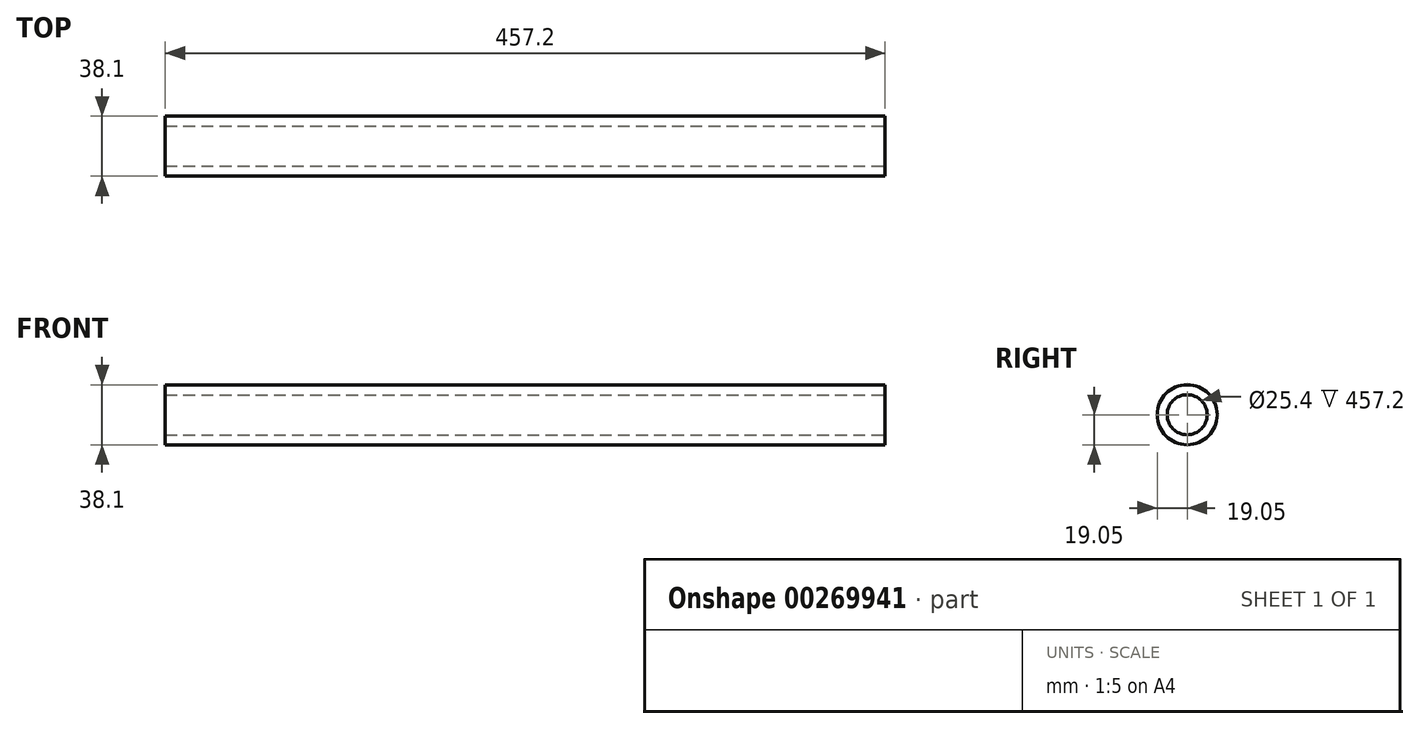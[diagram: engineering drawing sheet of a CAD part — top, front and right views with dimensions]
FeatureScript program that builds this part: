
annotation { "Feature Type Name" : "Feature", "Feature Type Description" : "" }
export const myFeature = defineFeature(function(context is Context, id is Id, definition is map)
    precondition{}
    {
        {
            var Q0;
            Q0=qCreatedBy(makeId("Right.planeOp"),FACE);
            var sketch = newSketch(context, id + "F0", { "sketchPlane" : qUnion([Q0])});
            skCircle(sketch, "E0", {"center": v(0, 0) * mm, "radius": 19.05 * mm});
            skSolve(sketch);
        }
        {
            var Q0;
            Q0=qSketchRegion(id+"F0",true);
            extrude(context, id + "F1", {"entities" : qUnion([Q0]), "depth" : 457.2 * mm});
        }
        {
            var Q0;
            Q0=makeQuery(id+"F1.opExtrude","CAP_FACE",FACE,{"disambiguationData":[OSD([sQuery(id+"F0.wireOp",EDGE,"E0")])],"isStart":false});
            var sketch = newSketch(context, id + "F2", { "sketchPlane" : qUnion([Q0])});
            skCircle(sketch, "E1", {"center": v(0, 0) * mm, "radius": 12.7 * mm});
            skSolve(sketch);
        }
        {
            var Q0;
            Q0=qSketchRegion(id+"F2",true);
            extrude(context, id + "F3", {"entities" : qUnion([Q0]), "operationType" : NewBodyOperationType.REMOVE, "endBound" : BoundingType.THROUGH_ALL, "oppositeDirection" : true, "depth" : 25.4 * mm});
        }
    });
